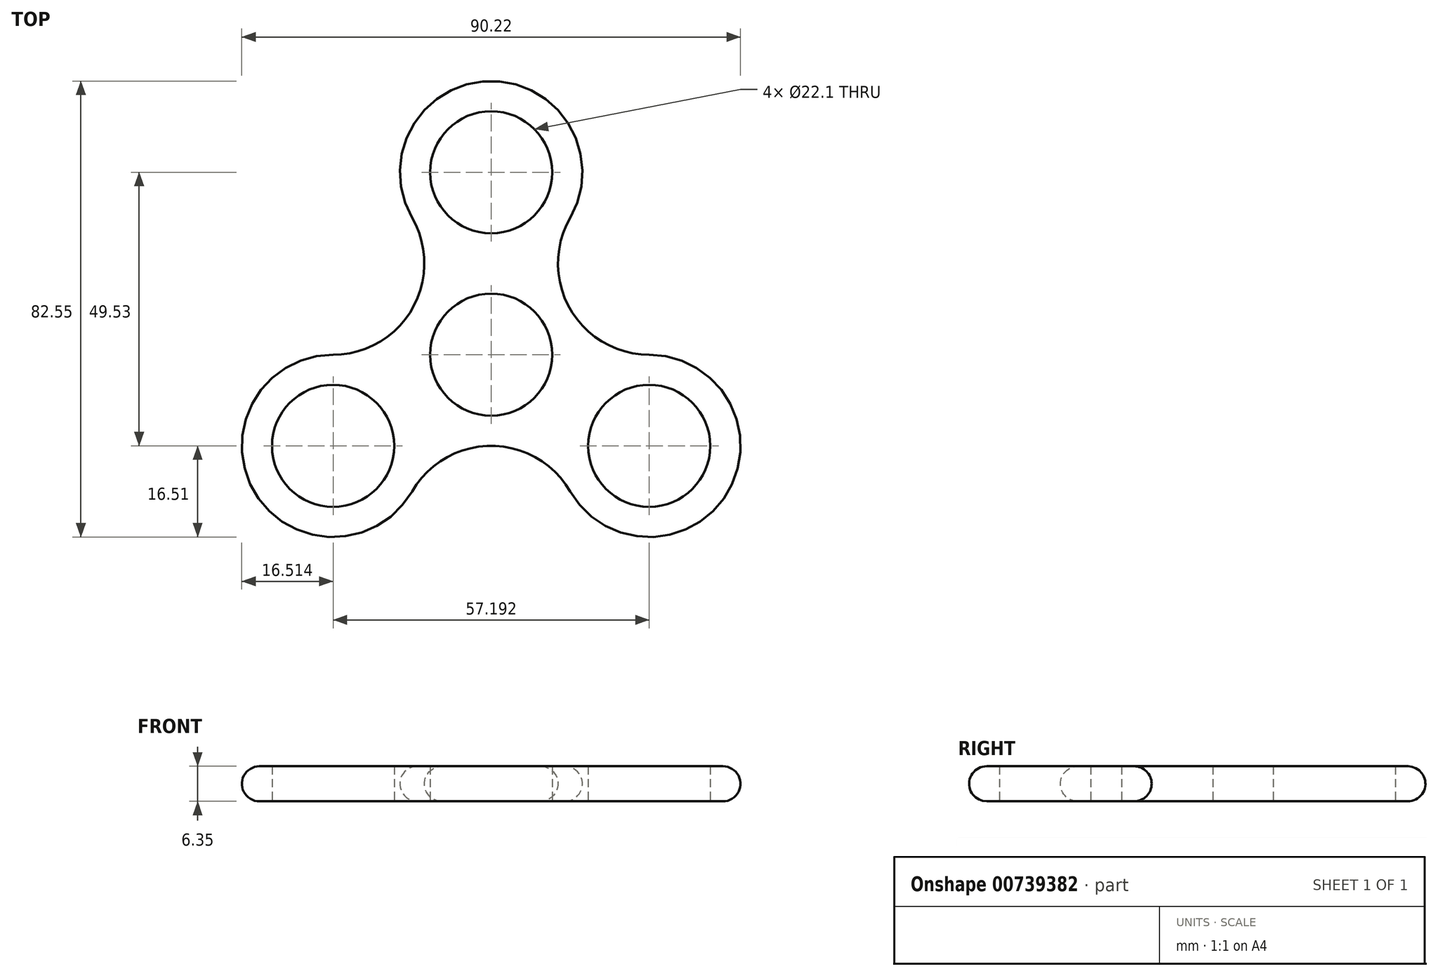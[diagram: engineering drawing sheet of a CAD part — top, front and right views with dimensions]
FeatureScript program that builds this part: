
annotation { "Feature Type Name" : "Feature", "Feature Type Description" : "" }
export const myFeature = defineFeature(function(context is Context, id is Id, definition is map)
    precondition{}
    {
        {
            var Q0;
            Q0=qCreatedBy(makeId("Top.planeOp"),FACE);
            var sketch = newSketch(context, id + "F0", { "sketchPlane" : qUnion([Q0])});
            skCircle(sketch, "E0", {"center": v(0, 0) * mm, "radius": 11.05 * mm});
            skLineSegment(sketch, "E1", {"start": v(0, 0) * mm, "end": v(0, 33.02) * mm});
            skCircle(sketch, "E2", {"center": v(0, 33.02) * mm, "radius": 11.05 * mm});
            skArc(sketch, "E3", {"start": v(14.3, 24.77) * mm, "mid": v(0, 49.53) * mm, "end": v(-14.3, 24.77) * mm});
            skArc(sketch, "E4.1.0", {"start": v(-28.6, 0) * mm, "mid": v(-42.9, -24.76) * mm, "end": v(-14.3, -24.77) * mm});
            skCircle(sketch, "E4.1.1", {"center": v(-28.6, -16.5) * mm, "radius": 11.05 * mm});
            skArc(sketch, "E4.2.0", {"start": v(14.3, -24.77) * mm, "mid": v(42.9, -24.77) * mm, "end": v(28.6, 0) * mm});
            skCircle(sketch, "E4.2.1", {"center": v(28.6, -16.51) * mm, "radius": 11.05 * mm});
            skLineSegment(sketch, "E5", {"start": v(0, 0) * mm, "end": v(-28.6, 16.51) * mm});
            skArc(sketch, "E6", {"start": v(-28.6, 0) * mm, "mid": v(-14.3, 8.26) * mm, "end": v(-14.3, 24.77) * mm});
            skArc(sketch, "E7.1.0", {"start": v(14.3, -24.77) * mm, "mid": v(0, -16.5) * mm, "end": v(-14.3, -24.76) * mm});
            skArc(sketch, "E7.2.0", {"start": v(14.3, 24.76) * mm, "mid": v(14.3, 8.25) * mm, "end": v(28.6, 0) * mm});
            skSolve(sketch);
        }
        {
            var Q0;
            Q0 = qSketchRegion(id + "F0", true);
            extrude(context, id + "F1", {"entities" : qUnion([Q0]), "depth" : 6.35 * mm, "offsetDistance" : 25.4 * mm});
        }
        {
            var Q0;
            Q0=makeQuery(id+"F1.opExtrude","CAP_EDGE",EDGE,{"disambiguationData":[OSD([sQuery(id+"F0.wireOp",EDGE,"E6")])],"isStart":false});
            var Q1;
            Q1=makeQuery(id+"F1.opExtrude","CAP_EDGE",EDGE,{"disambiguationData":[OSD([sQuery(id+"F0.wireOp",EDGE,"E3")])],"isStart":false});
            var Q2;
            Q2=makeQuery(id+"F1.opExtrude","CAP_EDGE",EDGE,{"disambiguationData":[OSD([sQuery(id+"F0.wireOp",EDGE,"E7.2.0")])],"isStart":false});
            var Q3;
            Q3=makeQuery(id+"F1.opExtrude","CAP_EDGE",EDGE,{"disambiguationData":[OSD([sQuery(id+"F0.wireOp",EDGE,"E4.2.0")])],"isStart":false});
            var Q4;
            Q4=makeQuery(id+"F1.opExtrude","CAP_EDGE",EDGE,{"disambiguationData":[OSD([sQuery(id+"F0.wireOp",EDGE,"E7.1.0")])],"isStart":false});
            var Q5;
            Q5=makeQuery(id+"F1.opExtrude","CAP_EDGE",EDGE,{"disambiguationData":[OSD([sQuery(id+"F0.wireOp",EDGE,"E4.1.0")])],"isStart":false});
            var Q6;
            Q6=makeQuery(id+"F1.opExtrude","CAP_EDGE",EDGE,{"disambiguationData":[OSD([sQuery(id+"F0.wireOp",EDGE,"E6")])],"isStart":true});
            var Q7;
            Q7=makeQuery(id+"F1.opExtrude","CAP_EDGE",EDGE,{"disambiguationData":[OSD([sQuery(id+"F0.wireOp",EDGE,"E3")])],"isStart":true});
            var Q8;
            Q8=makeQuery(id+"F1.opExtrude","SWEPT_FACE",FACE,{"disambiguationData":[OSD([sQuery(id+"F0.wireOp",EDGE,"E4.2.0")])]});
            var Q9;
            Q9=makeQuery(id+"F1.opExtrude","SWEPT_FACE",FACE,{"disambiguationData":[OSD([sQuery(id+"F0.wireOp",EDGE,"E4.1.0")])]});
            var Q10;
            Q10=makeQuery(id+"F1.opExtrude","CAP_EDGE",EDGE,{"disambiguationData":[OSD([sQuery(id+"F0.wireOp",EDGE,"E4.2.0")])],"isStart":true});
            var Q11;
            Q11=makeQuery(id+"F1.opExtrude","CAP_EDGE",EDGE,{"disambiguationData":[OSD([sQuery(id+"F0.wireOp",EDGE,"E7.1.0")])],"isStart":true});
            var Q12;
            Q12=makeQuery(id+"F1.opExtrude","CAP_EDGE",EDGE,{"disambiguationData":[OSD([sQuery(id+"F0.wireOp",EDGE,"E7.2.0")])],"isStart":true});
            var Q13;
            Q13=makeQuery(id+"F1.opExtrude","CAP_EDGE",EDGE,{"disambiguationData":[OSD([sQuery(id+"F0.wireOp",EDGE,"E4.1.0")])],"isStart":true});
            fillet(context, id + "F2", {"entities" : qUnion([Q0, Q1, Q2, Q3, Q4, Q5, Q6, Q7, Q8, Q9, Q10, Q11, Q12, Q13]), "radius" : 3.17 * mm, "tangentPropagation" : true, "allowEdgeOverflow" : false});
        }
    });
